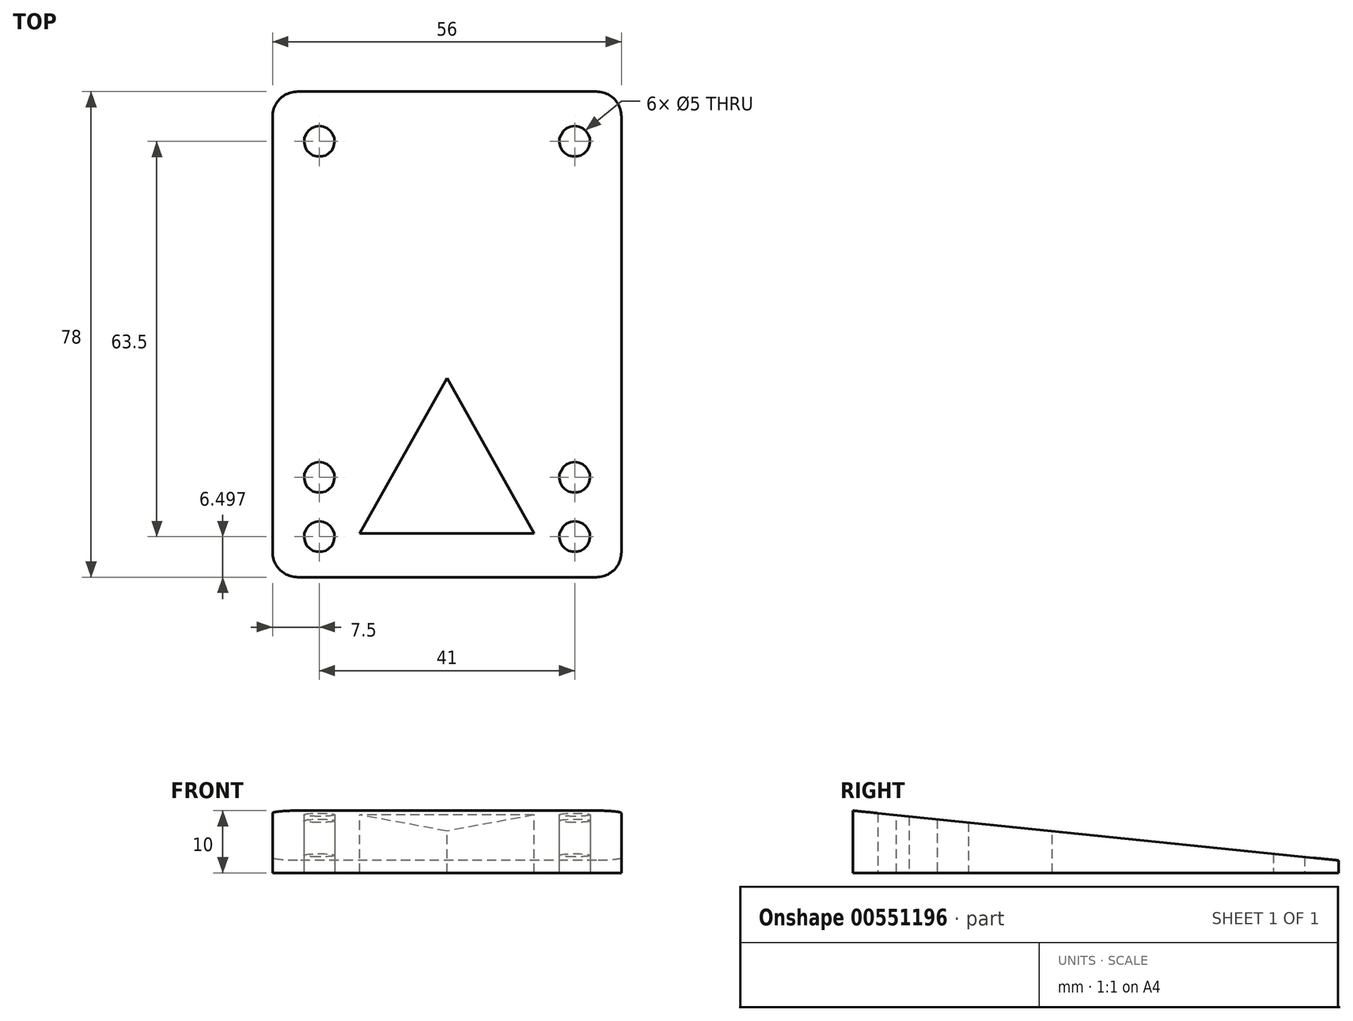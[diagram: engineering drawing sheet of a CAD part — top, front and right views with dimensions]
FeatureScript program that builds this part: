
annotation { "Feature Type Name" : "Feature", "Feature Type Description" : "" }
export const myFeature = defineFeature(function(context is Context, id is Id, definition is map)
    precondition{}
    {
        {
            var Q0;
            Q0=qCreatedBy(makeId("Top.planeOp"),FACE);
            var sketch = newSketch(context, id + "F0", { "sketchPlane" : qUnion([Q0])});
            skLineSegment(sketch, "E0.bottom", {"start": v(-18.85, 36.64) * mm, "end": v(29.15, 36.64) * mm});
            skLineSegment(sketch, "E0.top", {"start": v(-18.85, -41.36) * mm, "end": v(29.15, -41.36) * mm});
            skLineSegment(sketch, "E0.left", {"start": v(-22.85, 32.64) * mm, "end": v(-22.85, -37.36) * mm});
            skLineSegment(sketch, "E0.right", {"start": v(33.15, 32.64) * mm, "end": v(33.15, -37.36) * mm});
            skCircle(sketch, "E1", {"center": v(-15.35, 28.64) * mm, "radius": 2.5 * mm});
            skCircle(sketch, "E2", {"center": v(25.65, 28.64) * mm, "radius": 2.5 * mm});
            skCircle(sketch, "E3", {"center": v(-15.35, -34.86) * mm, "radius": 2.5 * mm});
            skCircle(sketch, "E4", {"center": v(25.65, -34.86) * mm, "radius": 2.5 * mm});
            skPoint(sketch, "E5.visualSharp", {"position": v(-22.85, 36.64) * mm});
            skArc(sketch, "E5.filletArc", {"start": v(-18.85, 36.64) * mm, "mid": v(-21.68, 35.47) * mm, "end": v(-22.85, 32.64) * mm});
            skPoint(sketch, "E6.visualSharp", {"position": v(33.15, 36.64) * mm});
            skArc(sketch, "E6.filletArc", {"start": v(33.15, 32.64) * mm, "mid": v(31.98, 35.47) * mm, "end": v(29.15, 36.64) * mm});
            skPoint(sketch, "E7.visualSharp", {"position": v(33.15, -41.36) * mm});
            skArc(sketch, "E7.filletArc", {"start": v(29.15, -41.36) * mm, "mid": v(31.98, -40.2) * mm, "end": v(33.15, -37.36) * mm});
            skPoint(sketch, "E8.visualSharp", {"position": v(-22.85, -41.36) * mm});
            skArc(sketch, "E8.filletArc", {"start": v(-22.85, -37.36) * mm, "mid": v(-21.68, -40.2) * mm, "end": v(-18.85, -41.36) * mm});
            skCircle(sketch, "E9", {"center": v(25.65, -25.34) * mm, "radius": 2.5 * mm});
            skCircle(sketch, "E10", {"center": v(-15.35, -25.34) * mm, "radius": 2.5 * mm});
            skSolve(sketch);
        }
        {
            var Q0;
            Q0=makeQuery(id+"F0.imprint","IMPRINT",FACE,{"disambiguationData":[TD([[makeQuery(id+"F0.imprint","IMPRINT",EDGE,{"derivedFrom":sQuery(id+"F0.wireOp",EDGE,"E0.bottom")}),-1.0]])]});
            extrude(context, id + "F1", {"entities" : qUnion([Q0]), "depth" : 20 * mm, "offsetDistance" : 25 * mm});
        }
        {
            var Q0;
            Q0=makeQuery(id+"F1.opExtrude","CAP_FACE",FACE,{"disambiguationData":[OSD([sQuery(id+"F0.wireOp",EDGE,"E0.bottom"),sQuery(id+"F0.wireOp",EDGE,"E0.top"),sQuery(id+"F0.wireOp",EDGE,"E0.left"),sQuery(id+"F0.wireOp",EDGE,"E0.right"),sQuery(id+"F0.wireOp",EDGE,"E1"),sQuery(id+"F0.wireOp",EDGE,"E2"),sQuery(id+"F0.wireOp",EDGE,"E3"),sQuery(id+"F0.wireOp",EDGE,"E4"),sQuery(id+"F0.wireOp",EDGE,"E5.filletArc"),sQuery(id+"F0.wireOp",EDGE,"E6.filletArc"),sQuery(id+"F0.wireOp",EDGE,"E7.filletArc"),sQuery(id+"F0.wireOp",EDGE,"E8.filletArc")])],"isStart":false});
            var sketch = newSketch(context, id + "F2", { "sketchPlane" : qUnion([Q0])});
            skLineSegment(sketch, "E11", {"start": v(-8.85, 31.64) * mm, "end": v(19.15, 31.64) * mm});
            skLineSegment(sketch, "E12", {"start": v(19.15, 31.64) * mm, "end": v(5.15, 6.64) * mm});
            skPoint(sketch, "E12.endSnap0", {"position": v(5.15, 31.64) * mm});
            skLineSegment(sketch, "E13", {"start": v(-8.85, 31.64) * mm, "end": v(5.15, 6.64) * mm});
            skLineSegment(sketch, "E14", {"start": v(-8.85, -34.36) * mm, "end": v(19.15, -34.36) * mm});
            skLineSegment(sketch, "E15", {"start": v(-8.85, -34.36) * mm, "end": v(5.15, -9.36) * mm});
            skLineSegment(sketch, "E16", {"start": v(5.15, -9.36) * mm, "end": v(19.15, -34.36) * mm});
            skLineSegment(sketch, "E17", {"start": v(-16.85, 23.91) * mm, "end": v(-9.85, 23.91) * mm});
            skLineSegment(sketch, "E18", {"start": v(-9.85, 23.91) * mm, "end": v(-0.85, 8.91) * mm});
            skLineSegment(sketch, "E19", {"start": v(-16.85, 23.91) * mm, "end": v(-16.85, 6.91) * mm});
            skLineSegment(sketch, "E20", {"start": v(-16.85, 6.91) * mm, "end": v(-0.85, 6.91) * mm});
            skLineSegment(sketch, "E21", {"start": v(-0.85, 8.91) * mm, "end": v(-0.85, 6.91) * mm});
            skSolve(sketch);
        }
        {
            var Q0;
            Q0=makeQuery(id+"F2.imprint","IMPRINT",FACE,{"disambiguationData":[TD([[makeQuery(id+"F2.imprint","IMPRINT",EDGE,{"derivedFrom":sQuery(id+"F2.wireOp",EDGE,"E14")}),1.0]])]});
            extrude(context, id + "F3", {"entities" : qUnion([Q0]), "operationType" : NewBodyOperationType.REMOVE, "oppositeDirection" : true, "depth" : 25 * mm});
        }
        {
            var Q0;
            Q0=qCreatedBy(makeId("Right.planeOp"),FACE);
            var sketch = newSketch(context, id + "F4", { "sketchPlane" : qUnion([Q0])});
            skLineSegment(sketch, "E22", {"start": v(36.64, 20) * mm, "end": v(-41.36, 20) * mm});
            skLineSegment(sketch, "E23", {"start": v(-41.36, 10) * mm, "end": v(36.64, 2) * mm});
            skLineSegment(sketch, "E24", {"start": v(36.64, 2) * mm, "end": v(36.64, 20) * mm});
            skLineSegment(sketch, "E25", {"start": v(-41.36, 0) * mm, "end": v(-41.36, 20) * mm, "construction": true});
            skLineSegment(sketch, "E26", {"start": v(36.64, 0) * mm, "end": v(36.64, 20) * mm, "construction": true});
            skLineSegment(sketch, "E27", {"start": v(-41.36, 20) * mm, "end": v(-41.36, 10) * mm});
            skSolve(sketch);
        }
        {
            var Q0;
            Q0 = qSketchRegion(id + "F4", true);
            extrude(context, id + "F5", {"entities" : qUnion([Q0]), "operationType" : NewBodyOperationType.REMOVE, "endBound" : BoundingType.THROUGH_ALL, "depth" : 25 * mm, "offsetDistance" : 25 * mm, "hasSecondDirection" : true, "secondDirectionBound" : SecondDirectionBoundingType.THROUGH_ALL, "secondDirectionOppositeDirection" : true, "secondDirectionDepth" : 25 * mm});
        }
    });
